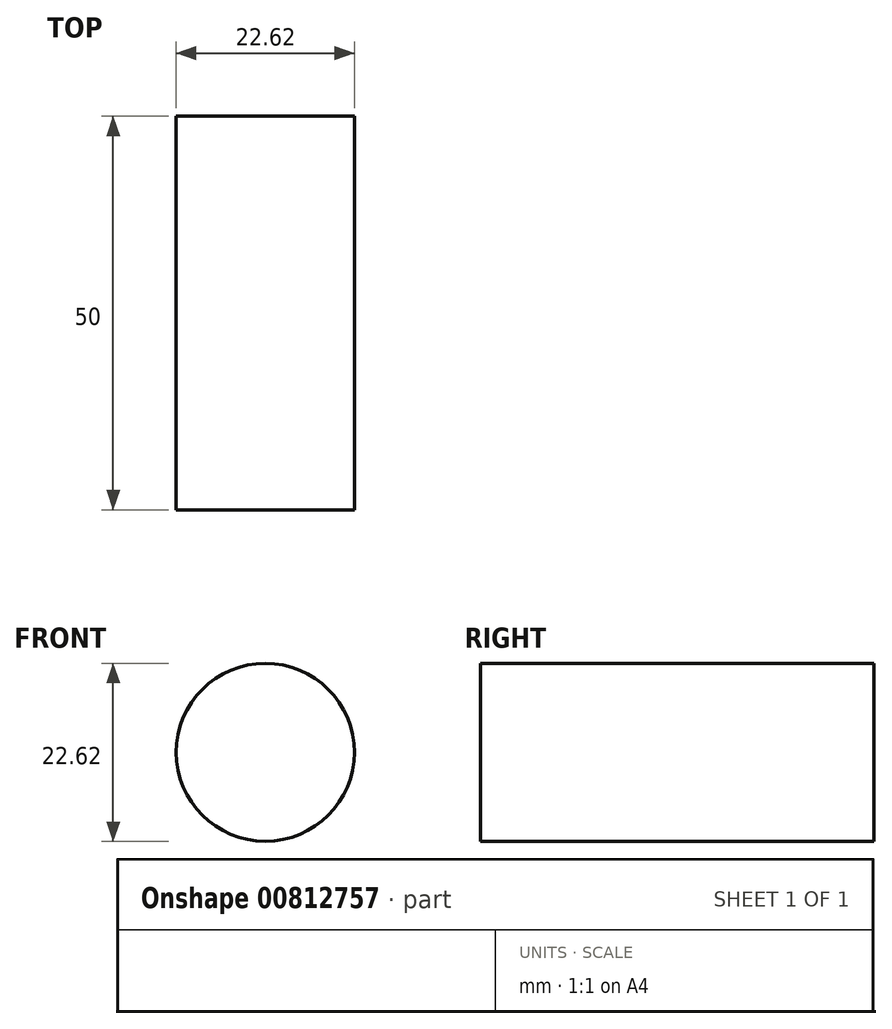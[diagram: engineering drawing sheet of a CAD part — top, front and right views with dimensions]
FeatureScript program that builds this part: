
annotation { "Feature Type Name" : "Feature", "Feature Type Description" : "" }
export const myFeature = defineFeature(function(context is Context, id is Id, definition is map)
    precondition{}
    {
        {
            var Q0;
            Q0=qCreatedBy(makeId("Front.planeOp"),FACE);
            var sketch = newSketch(context, id + "F0", { "sketchPlane" : qUnion([Q0])});
            skCircle(sketch, "E0", {"center": v(0, 0) * mm, "radius": 11.3 * mm});
            skSolve(sketch);
        }
        {
            var Q0;
            Q0=makeQuery(id+"F0.imprint","IMPRINT",FACE,{"disambiguationData":[TD([[makeQuery(id+"F0.imprint","IMPRINT",EDGE,{"derivedFrom":sQuery(id+"F0.wireOp",EDGE,"E0")}),1.0]])]});
            extrude(context, id + "F1", {"entities" : qUnion([Q0]), "depth" : 50 * mm, "offsetDistance" : 25 * mm});
        }
    });
